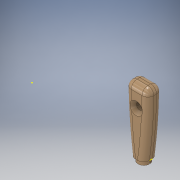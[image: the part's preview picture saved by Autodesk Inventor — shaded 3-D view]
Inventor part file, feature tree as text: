
AUTODESK INVENTOR PART (.ipt)
format: ipt  version: 2018 (Build 220112000, 112)  size: 211,456 bytes
history: native  units: in
note: dims shown in document units (in); Inventor stores cm internally (conversion verified against a paired STEP export)
features: sketch x6, extrude x2, hole x2, fillet x1, plane x1, revolve x1
ambient origin geometry x8: Origin, YZ Plane, XZ Plane, XY Plane, X Axis, Y Axis, Z Axis, Center Point
bodies: Solid1 (feature_tree)
feature tree (13):
  sketch  "Sketch1"  dims[d0=1.1525in d2=0.7in d3=0.739in d4=0.0in]
  extrude  "Extrusion1"  Depth=0.7in
  fillet  "Fillet1"  Radius=0.739in
  sketch  "Sketch2"  dims[d5=0.3in d11=90.0deg]
  plane  "Work Plane1"
  revolve  "Revolution2"  Angle=90.0deg
  extrude  "Extrusion2"  TaperAngle=90.0deg  [1 undecoded]
  hole  "Hole1"  [1 undecoded]
  hole  "Hole2"  [1 undecoded]
  sketch  "Sketch3"  dims[d14=3.0055in d15=90.0deg]
  sketch  "Sketch4"  dims[d17=0.145in d18=0.05in]
  sketch  "Sketch5"  dims[d19=0.639in d20=0.0in d23=0.6565in]
  sketch  "Sketch6"  dims[d24=0.33in d25=0.75in d26=0.645in d27=0.25in d28=0.5635in d29=1.0in d30=0.8108in d31=0.33in d32=0.75in d33=0.7075in d34=0.25in d35=0.5635in d36=1.0in d37=0.8108in]
note: 3 required parameter values undecoded (feature->parameter linkage not recoverable at this tier; creation-order binding heuristic only, values carry confidence <= 0.55)
